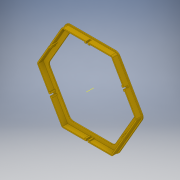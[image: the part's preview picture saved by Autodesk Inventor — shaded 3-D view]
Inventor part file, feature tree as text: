
AUTODESK INVENTOR PART (.ipt)
format: ipt  version: 2019 (Build 230136000, 136)  size: 526,336 bytes
history: native  units: mm
features: extrude x5, sketch x5, projected_geometry x3, fillet x2, other x1, pattern_circular x1
ambient origin geometry x8: Origin, YZ Plane, XZ Plane, XY Plane, X Axis, Y Axis, Z Axis, Center Point
bodies: Solid1 (feature_tree)
feature tree (17):
  extrude  "Extrusion1"  Depth=2.0mm
  extrude  "Extrusion5"  Depth=2.0mm
  extrude  "Extrusion6"  Depth=10.0mm
  fillet  "Fillet1"  [1 undecoded]
  fillet  "Fillet2"  Radius=8.0mm
  extrude  "Extrusion7"  TaperAngle=0.0deg  [1 undecoded]
  extrude  "Extrusion8"  Depth=4.0mm
  other  "Work Axis2"
  pattern_circular  "Circular Pattern1"  [2 undecoded]
  sketch  "Sketch1"  dims[d0=175.0mm d1=2.0mm]
  sketch  "Sketch5"  dims[d2=0.0mm d15=2.0mm]
  projected_geometry  "Projected Loop4"
  sketch  "Sketch7"  dims[d16=2.0mm d17=10.0mm d18=0.0mm d19=8.0mm]
  projected_geometry  "Projected Loop6"
  sketch  "Sketch8"  dims[d20=7.0mm d21=0.0mm]
  sketch  "Sketch9"  dims[d22=10.0mm d23=4.0mm d24=10.0mm d25=3.3mm d26=7.5mm d27=0.0mm d28=4.0mm d29=3.0mm d30=5.0mm d31=0.0mm d32=60.0mm d33=360.0deg]
  projected_geometry  "Projected Loop7"
note: 4 required parameter values undecoded (feature->parameter linkage not recoverable at this tier; creation-order binding heuristic only, values carry confidence <= 0.55)
